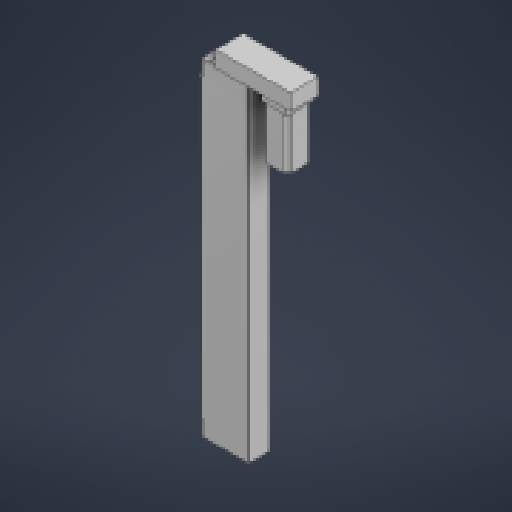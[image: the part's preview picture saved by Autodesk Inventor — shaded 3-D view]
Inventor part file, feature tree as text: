
AUTODESK INVENTOR PART (.ipt)
format: ipt  version: 2025 (Build 290162000, 162)  size: 179,200 bytes
history: native  units: in
note: dims shown in document units (in); Inventor stores cm internally (conversion verified against a paired STEP export)
features: extrude x1, sketch x1
ambient origin geometry x8: Origin, YZ Plane, XZ Plane, XY Plane, X Axis, Y Axis, Z Axis, Center Point
bodies: Solid1 (feature_tree), Solid2 (feature_tree), Solid3 (feature_tree), Body1 (feature_tree), Body5 (feature_tree), Body6 (feature_tree)
feature tree (2):
  extrude  "Extrusion1"  [1 undecoded]
  sketch  "Sketch1"  dims[d0=0.0394in d1=0.0in]
note: 1 required parameter value undecoded (feature->parameter linkage not recoverable at this tier; creation-order binding heuristic only, values carry confidence <= 0.55)
